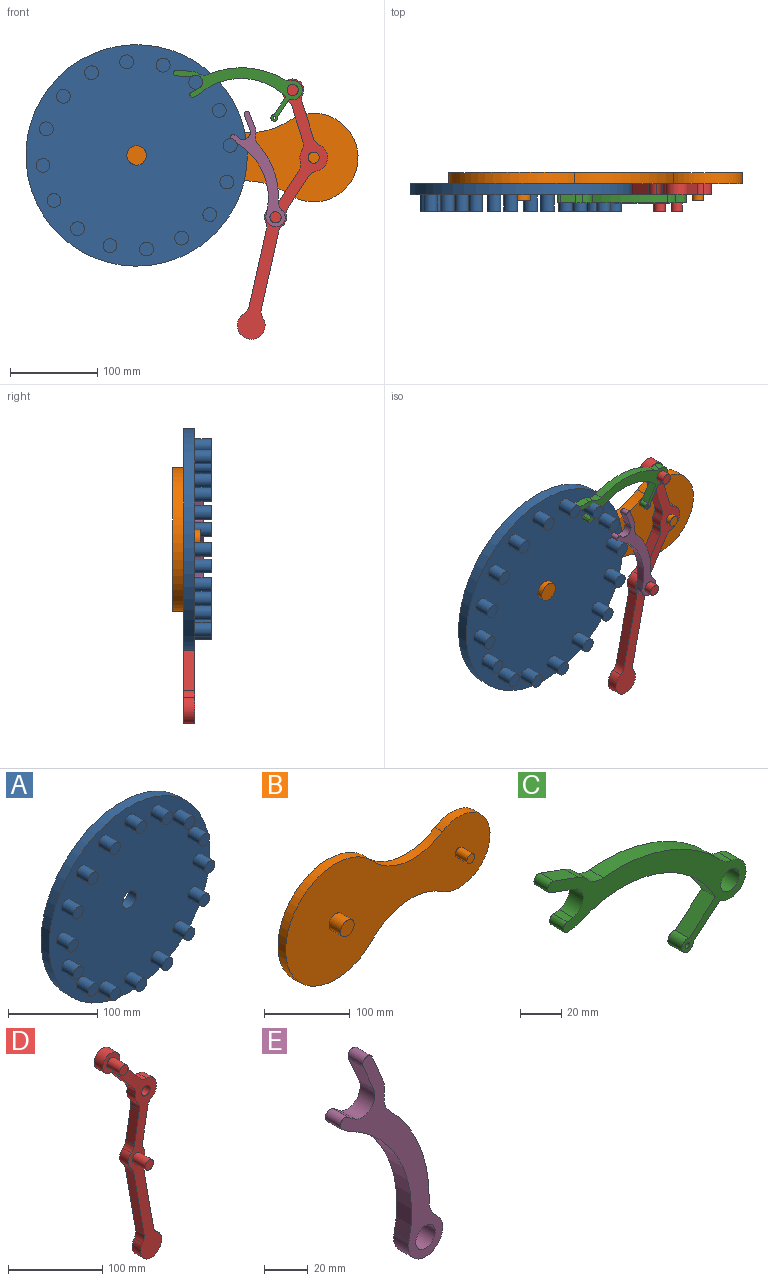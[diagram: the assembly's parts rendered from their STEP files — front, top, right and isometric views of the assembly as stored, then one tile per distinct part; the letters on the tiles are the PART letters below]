
ASSEMBLY  parts=5 mates=4
PART A: 36 faces, bbox 254x31.8x254 mm
  f0: cylinder r=11.11mm len=22.23mm, axis (0,1,0), area 886.7mm2, adj f2,f3
  f1: cylinder r=127mm len=254mm, axis (0,1,0), area 10134.1mm2, adj f2,f3
  f2: plane 254x254mm, normal (0,-1,0), area 47115.9mm2, adj f0,f1,f4,f6,f8,f10,f12,f14
  f3: plane 254x254mm, normal (0,1,0), area 50282.8mm2, adj f0,f1
  f4: cylinder r=7.94mm len=19.05mm, axis (0,1,0), area 950.1mm2, adj f2,f5
  f5: plane 15.88x15.88mm, normal (0,-1,0), area 197.9mm2, adj f4
  f6: cylinder r=7.94mm len=19.05mm, axis (0,1,0), area 950.1mm2, adj f2,f7
  f7: plane 15.88x15.88mm, normal (0,-1,0), area 197.9mm2, adj f6
  f8: cylinder r=7.94mm len=19.05mm, axis (0,1,0), area 950.1mm2, adj f2,f9
  f9: plane 15.88x15.88mm, normal (0,-1,0), area 197.9mm2, adj f8
  f10: cylinder r=7.94mm len=19.05mm, axis (0,1,0), area 950.1mm2, adj f2,f11
  f11: plane 15.88x15.88mm, normal (0,-1,0), area 197.9mm2, adj f10
  f12: cylinder r=7.94mm len=19.05mm, axis (0,1,0), area 950.1mm2, adj f2,f13
  f13: plane 15.88x15.88mm, normal (0,-1,0), area 197.9mm2, adj f12
  f14: cylinder r=7.94mm len=19.05mm, axis (0,1,0), area 950.1mm2, adj f2,f15
  f15: plane 15.88x15.88mm, normal (0,-1,0), area 197.9mm2, adj f14
  f16: cylinder r=7.94mm len=19.05mm, axis (0,1,0), area 950.1mm2, adj f2,f17
  f17: plane 15.88x15.88mm, normal (0,-1,0), area 197.9mm2, adj f16
  f18: cylinder r=7.94mm len=19.05mm, axis (0,1,0), area 950.1mm2, adj f2,f19
  f19: plane 15.88x15.88mm, normal (0,-1,0), area 197.9mm2, adj f18
  f20: cylinder r=7.94mm len=19.05mm, axis (0,1,0), area 950.1mm2, adj f2,f21
  f21: plane 15.88x15.88mm, normal (0,-1,0), area 197.9mm2, adj f20
  f22: cylinder r=7.94mm len=19.05mm, axis (0,1,0), area 950.1mm2, adj f2,f23
  f23: plane 15.88x15.88mm, normal (0,-1,0), area 197.9mm2, adj f22
  f24: cylinder r=7.94mm len=19.05mm, axis (0,1,0), area 950.1mm2, adj f2,f25
  f25: plane 15.88x15.88mm, normal (0,-1,0), area 197.9mm2, adj f24
  f26: cylinder r=7.94mm len=19.05mm, axis (0,1,0), area 950.1mm2, adj f2,f27
  f27: plane 15.88x15.88mm, normal (0,-1,0), area 197.9mm2, adj f26
  f28: cylinder r=7.94mm len=19.05mm, axis (0,1,0), area 950.1mm2, adj f2,f29
  f29: plane 15.88x15.88mm, normal (0,-1,0), area 197.9mm2, adj f28
  f30: cylinder r=7.94mm len=19.05mm, axis (0,1,0), area 950.1mm2, adj f2,f31
  f31: plane 15.88x15.88mm, normal (0,-1,0), area 197.9mm2, adj f30
  f32: cylinder r=7.94mm len=19.05mm, axis (0,1,0), area 950.1mm2, adj f2,f33
  f33: plane 15.88x15.88mm, normal (0,-1,0), area 197.9mm2, adj f32
  f34: cylinder r=7.94mm len=19.05mm, axis (0,1,0), area 950.1mm2, adj f2,f35
  f35: plane 15.88x15.88mm, normal (0,-1,0), area 197.9mm2, adj f34
PART B: 10 faces, bbox 336.6x31.8x165.1 mm
  f0: cylinder r=82.55mm len=165.1mm, axis (0,-1,0), area 5023mm2, adj f1,f3,f4,f5
  f1: cylinder r=88.9mm len=114.64mm, axis (0,-1,0), area 1593.2mm2, adj f0,f2,f4,f5
  f2: cylinder r=50.8mm len=101.6mm, axis (0,-1,0), area 2783.4mm2, adj f1,f3,f4,f5
  f3: cylinder r=88.9mm len=114.3mm, axis (0,-1,0), area 1593.2mm2, adj f0,f2,f4,f5
  f4: plane 336.55x165.1mm, normal (0,1,0), area 34386mm2, adj f0,f1,f2,f3
  f5: plane 336.55x165.1mm, normal (0,-1,0), area 33871.3mm2, adj f0,f1,f2,f3,f7,f9
  f6: plane 22.23x22.23mm, normal (0,-1,0), area 387.9mm2, adj f7
  f7: cylinder r=11.11mm len=22.23mm, axis (0,1,0), area 1330.1mm2, adj f5,f6
  f8: plane 12.7x12.7mm, normal (0,-1,0), area 126.7mm2, adj f9
  f9: cylinder r=6.35mm len=19.05mm, axis (0,1,0), area 760.1mm2, adj f5,f8
PART C: 21 faces, bbox 136.7x9.5x88.6 mm
  f0: plane 18.45x15.46mm, normal (0.64,0,-0.77), area 229.3mm2, adj f1,f17,f19,f20
  f1: cylinder r=11.11mm len=22.13mm, axis (0,1,0), area 388.2mm2, adj f0,f2,f19,f20
  f2: cylinder r=12.7mm len=9.53mm, axis (0,1,0), area 82.3mm2, adj f1,f3,f19,f20
  f3: cylinder r=98.18mm len=81.14mm, axis (0,1,0), area 853.7mm2, adj f2,f4,f19,f20
  f4: cylinder r=12.7mm len=11.04mm, axis (0,1,0), area 118.2mm2, adj f3,f5,f19,f20
  f5: cylinder r=14.8mm len=9.53mm, axis (0,1,0), area 74.1mm2, adj f4,f6,f19,f20
  f6: plane 16.7x9.53mm, normal (0.34,0,0.94), area 169.4mm2, adj f5,f7,f19,f20
  f7: cylinder r=3.17mm len=9.53mm, axis (0,1,0), area 95mm2, adj f6,f8,f19,f20
  f8: plane 16.7x9.53mm, normal (-0.34,0,-0.94), area 169.4mm2, adj f7,f9,f19,f20
  f9: cylinder r=8.45mm len=16.25mm, axis (0,1,0), area 210.6mm2, adj f8,f10,f19,f20
  f10: plane 9.53x3.95mm, normal (-0.17,0,0.98), area 38.2mm2, adj f9,f11,f19,f20
  f11: cylinder r=3.17mm len=9.53mm, axis (0,1,0), area 95mm2, adj f10,f12,f19,f20
  f12: plane 9.53x3.95mm, normal (0.17,0,-0.98), area 38.2mm2, adj f11,f13,f19,f20
  f13: cylinder r=14.8mm len=9.53mm, axis (0,1,0), area 34.6mm2, adj f12,f14,f19,f20
  f14: cylinder r=73.03mm len=93.77mm, axis (0,1,0), area 1035.7mm2, adj f13,f15,f19,f20
  f15: plane 18.45x15.46mm, normal (-0.64,0,0.77), area 229.3mm2, adj f14,f17,f19,f20
  f16: cylinder r=6.35mm len=12.7mm, axis (0,1,0), area 380mm2, adj f19,f20
  f17: cylinder r=3.97mm len=9.53mm, axis (0,1,0), area 188.9mm2, adj f0,f15,f19,f20
  f18: cylinder r=1.59mm len=9.53mm, axis (0,1,0), area 95mm2, adj f19,f20
  f19: plane 136.65x88.63mm, normal (0,-1,0), area 2069.4mm2, adj f0,f1,f2,f3,f4,f5,f6,f7
  f20: plane 136.65x88.63mm, normal (0,1,0), area 2069.4mm2, adj f0,f1,f2,f3,f4,f5,f6,f7
PART D: 31 faces, bbox 88.8x31.8x296 mm
  f0: cylinder r=12.7mm len=19.46mm, axis (0,1,0), area 281.6mm2, adj f8,f18,f19,f30
  f1: cylinder r=12.7mm len=25.4mm, axis (0,1,0), area 739.8mm2, adj f2,f16,f18,f19
  f2: cylinder r=12.7mm len=12.7mm, axis (0,1,0), area 116.6mm2, adj f1,f3,f18,f19
  f3: plane 33.08x27.76mm, normal (-0.77,0,-0.64), area 548.4mm2, adj f2,f4,f18,f19
  f4: cylinder r=12.7mm len=12.7mm, axis (0,1,0), area 135.7mm2, adj f3,f5,f18,f19
  f5: cylinder r=15.88mm len=12.7mm, axis (0,1,0), area 163.2mm2, adj f4,f6,f18,f19
  f6: cylinder r=12.7mm len=12.7mm, axis (0,1,0), area 135.7mm2, adj f5,f7,f18,f19
  f7: plane 42.53x12.7mm, normal (-0.98,0,0.17), area 548.4mm2, adj f6,f8,f18,f19
  f8: cylinder r=12.7mm len=12.7mm, axis (0,1,0), area 116.6mm2, adj f0,f7,f18,f19
  f9: cylinder r=12.7mm len=12.7mm, axis (0,1,0), area 169mm2, adj f10,f18,f19,f24
  f10: cylinder r=12.7mm len=12.7mm, axis (0,1,0), area 116.6mm2, adj f9,f11,f18,f19
  f11: plane 42.53x12.7mm, normal (0.98,0,-0.17), area 548.4mm2, adj f10,f12,f18,f19
  f12: cylinder r=12.7mm len=12.7mm, axis (0,1,0), area 135.7mm2, adj f11,f13,f18,f19
  f13: cylinder r=15.88mm len=29.36mm, axis (0,1,0), area 515.1mm2, adj f12,f14,f18,f19
  f14: cylinder r=12.7mm len=12.7mm, axis (0,1,0), area 135.7mm2, adj f13,f15,f18,f19
  f15: plane 33.08x27.76mm, normal (0.77,0,0.64), area 548.4mm2, adj f14,f16,f18,f19
  f16: cylinder r=12.7mm len=12.7mm, axis (0,1,0), area 116.6mm2, adj f1,f15,f18,f19
  f17: cylinder r=6.35mm len=12.7mm, axis (0,1,0), area 506.7mm2, adj f18,f19
  f18: plane 295.96x88.76mm, normal (0,-1,0), area 5059.9mm2, adj f0,f1,f2,f3,f4,f5,f6,f7
  f19: plane 295.96x88.76mm, normal (0,1,0), area 5313.2mm2, adj f0,f1,f2,f3,f4,f5,f6,f7
  f20: cylinder r=6.35mm len=19.05mm, axis (0,1,0), area 760.1mm2, adj f18,f21
  f21: plane 12.7x12.7mm, normal (0,-1,0), area 126.7mm2, adj f20
  f22: cylinder r=6.35mm len=19.05mm, axis (0,1,0), area 760.1mm2, adj f18,f23
  f23: plane 12.7x12.7mm, normal (0,-1,0), area 126.7mm2, adj f22
  f24: cylinder r=12.7mm len=12.7mm, axis (0,1,0), area 108.7mm2, adj f9,f18,f19,f25
  f25: plane 89.21x15.73mm, normal (0.98,0,0.17), area 1150.4mm2, adj f18,f19,f24,f26
  f26: cylinder r=12.7mm len=12.7mm, axis (0,1,0), area 129.5mm2, adj f18,f19,f25,f27
  f27: cylinder r=15.88mm len=31.75mm, axis (0,1,0), area 957.2mm2, adj f18,f19,f26,f28
  f28: cylinder r=12.7mm len=12.7mm, axis (0,1,0), area 129.5mm2, adj f18,f19,f27,f29
  f29: plane 89.21x15.73mm, normal (-0.98,0,-0.17), area 1150.4mm2, adj f18,f19,f28,f30
  f30: cylinder r=12.7mm len=12.7mm, axis (0,1,0), area 108.7mm2, adj f0,f18,f19,f29
PART E: 16 faces, bbox 66.5x9.5x131.3 mm
  f0: cylinder r=11.11mm len=22.23mm, axis (0,1,0), area 449.5mm2, adj f1,f13,f14,f15
  f1: cylinder r=12.7mm len=10.08mm, axis (0,1,0), area 109.3mm2, adj f0,f2,f14,f15
  f2: cylinder r=87.23mm len=63.57mm, axis (0,1,0), area 670.7mm2, adj f1,f3,f14,f15
  f3: cylinder r=12.7mm len=11.24mm, axis (0,1,0), area 116.6mm2, adj f2,f4,f14,f15
  f4: cylinder r=14.8mm len=9.53mm, axis (0,1,0), area 82.2mm2, adj f3,f5,f14,f15
  f5: plane 16.34x9.53mm, normal (0.92,0,0.39), area 169.4mm2, adj f4,f6,f14,f15
  f6: cylinder r=3.17mm len=9.53mm, axis (0,1,0), area 95mm2, adj f5,f7,f14,f15
  f7: plane 16.34x9.53mm, normal (-0.92,0,-0.39), area 169.4mm2, adj f6,f8,f14,f15
  f8: cylinder r=8.45mm len=13.5mm, axis (0,1,0), area 210.6mm2, adj f7,f9,f14,f15
  f9: plane 9.53x4.06mm, normal (0.6,0,0.8), area 48.2mm2, adj f8,f10,f14,f15
  f10: cylinder r=3.17mm len=9.53mm, axis (0,1,0), area 95mm2, adj f9,f11,f14,f15
  f11: plane 9.53x4.06mm, normal (-0.6,0,-0.8), area 48.2mm2, adj f10,f13,f14,f15
  f12: cylinder r=6.35mm len=12.7mm, axis (0,1,0), area 380mm2, adj f14,f15
  f13: cylinder r=73.03mm len=81.79mm, axis (0,1,0), area 932.3mm2, adj f0,f11,f14,f15
  f14: plane 131.3x66.51mm, normal (0,-1,0), area 1703.1mm2, adj f0,f1,f2,f3,f4,f5,f6,f7
  f15: plane 131.3x66.51mm, normal (0,1,0), area 1703.1mm2, adj f0,f1,f2,f3,f4,f5,f6,f7
PLACE A rot(axis=(0,-1,0),6.1deg) t=(0,0,0)mm
PLACE B at identity fixed
PLACE C rot(axis=(0,-1,0),16.7deg) t=(51.62,0,-25.61)mm
PLACE D rot(axis=(0,1,0),22.7deg) t=(16.67,0,78.11)mm
PLACE E rot(axis=(0,1,0),2.3deg) t=(20.75,0,-10.46)mm
MATE revolute C.f1 <-> D.f1  axis (0,1,0) through (178.98,-12.7,75.05)mm
MATE revolute A.f0 <-> B.f0  axis (0,1,0) through (0,0,0)mm
MATE revolute E.f0 <-> D.f0  axis (0,1,0) through (159.33,-12.7,-70.96)mm
MATE revolute D.f5 <-> B.f2  axis (0,1,0) through (203.2,0,-2.54)mm
